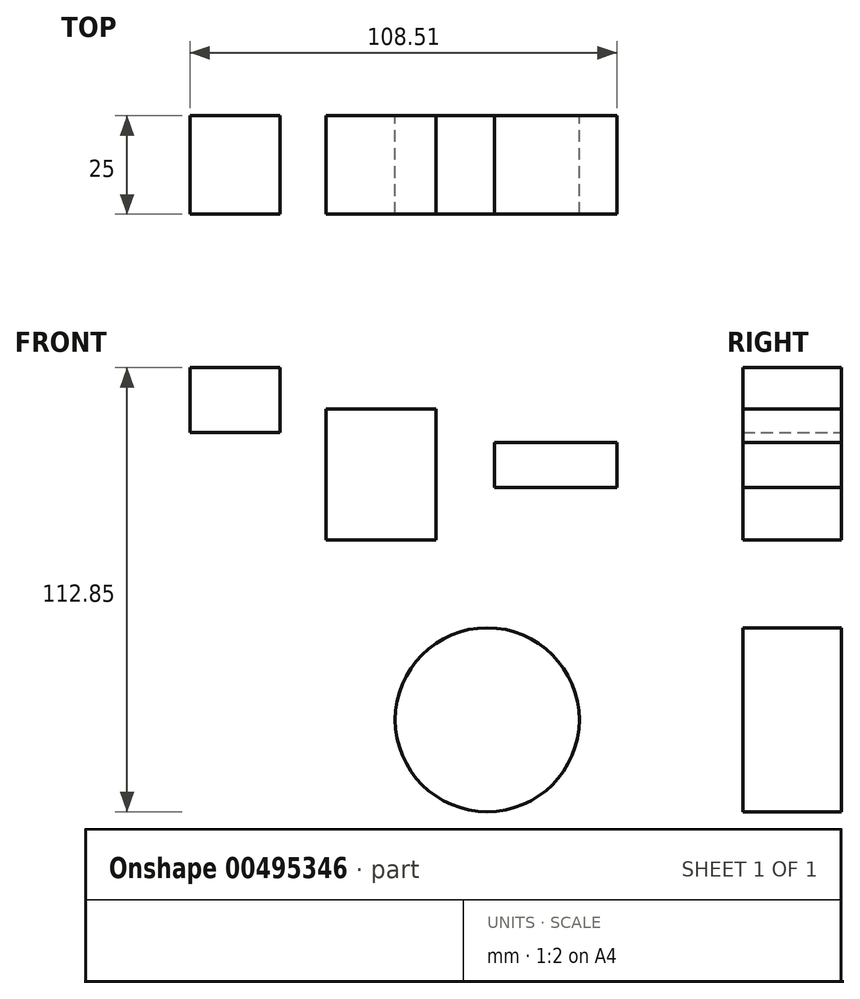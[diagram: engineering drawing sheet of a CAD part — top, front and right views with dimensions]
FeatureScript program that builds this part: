
annotation { "Feature Type Name" : "Feature", "Feature Type Description" : "" }
export const myFeature = defineFeature(function(context is Context, id is Id, definition is map)
    precondition{}
    {
        {
            var Q0;
            Q0=qCreatedBy(makeId("Front.planeOp"),FACE);
            var sketch = newSketch(context, id + "F0", { "sketchPlane" : qUnion([Q0])});
            skLineSegment(sketch, "E0.bottom", {"start": v(-118.66, 57.27) * mm, "end": v(-95.81, 57.27) * mm});
            skLineSegment(sketch, "E0.top", {"start": v(-118.66, 40.77) * mm, "end": v(-95.81, 40.77) * mm});
            skLineSegment(sketch, "E0.left", {"start": v(-118.66, 57.27) * mm, "end": v(-118.66, 40.77) * mm});
            skLineSegment(sketch, "E0.right", {"start": v(-95.81, 57.27) * mm, "end": v(-95.81, 40.77) * mm});
            skLineSegment(sketch, "E1.bottom", {"start": v(-84.07, 46.8) * mm, "end": v(-56.16, 46.8) * mm});
            skLineSegment(sketch, "E1.top", {"start": v(-84.07, 13.48) * mm, "end": v(-56.16, 13.48) * mm});
            skLineSegment(sketch, "E1.left", {"start": v(-84.07, 46.8) * mm, "end": v(-84.07, 13.48) * mm});
            skLineSegment(sketch, "E1.right", {"start": v(-56.16, 46.8) * mm, "end": v(-56.16, 13.48) * mm});
            skLineSegment(sketch, "E2.bottom", {"start": v(-41.24, 26.8) * mm, "end": v(-10.15, 26.8) * mm});
            skLineSegment(sketch, "E2.top", {"start": v(-41.24, 38.23) * mm, "end": v(-10.15, 38.23) * mm});
            skLineSegment(sketch, "E2.left", {"start": v(-41.24, 26.8) * mm, "end": v(-41.24, 38.23) * mm});
            skLineSegment(sketch, "E2.right", {"start": v(-10.15, 26.8) * mm, "end": v(-10.15, 38.23) * mm});
            skCircle(sketch, "E3", {"center": v(-43.15, -32.2) * mm, "radius": 23.38 * mm});
            skSolve(sketch);
        }
        {
            var Q0;
            Q0 = qSketchRegion(id + "F0", true);
            extrude(context, id + "F1", {"entities" : qUnion([Q0]), "depth" : 25 * mm});
        }
    });
